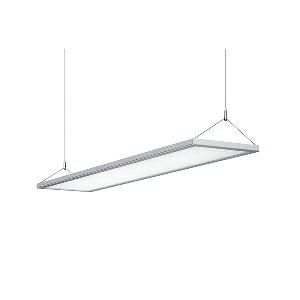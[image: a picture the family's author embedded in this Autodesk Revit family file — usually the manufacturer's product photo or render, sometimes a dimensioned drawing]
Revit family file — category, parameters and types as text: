
# Revit family: idoo_pendant_-_ipp_7000_840_d_00688760_aaad
name_source: partatom
category: Lighting Fixtures
units: mm (PartAtom-declared; Revit-internal decimal feet)

## family parameters
Cut with Voids When Loaded = No
Host = Face
Light Source = No
Part Type = Normal
Room Calculation Point = No
Round Connector Dimension = Use Diameter
Shared = No

## types (1)
- IDOO.pendant - IPP 7000/840/D (1 x LED, 7000 lm, 4000K)
    Apparent Load = 49 VA
    Approval mark = CE
    CIE Flux Codes = 55 85 96 33 100
    Color Rendering = 80-89
    Color Temperature = 4000K
    Control Gear = Electronic ballast
    Default Elevation = 1800 mm
    Description = IPP 7000/840/D|Suspended luminaire|light source: LED|connected load: 220-240V, 50/60Hz|Power consumption: approx. 49 W|standby: approx. 0,30|luminous flux: 7000 lm|luminous efficacy: 142 lm/W|light distribution: Direct/indirect|direct ratio: approx. 34 %|colour temperature: Cold white, ca. 4000 K|color rendering index (CRI): >= 80|chromaticity tolerance:  3 SDCM|System of protection: IP 20|technology: Continuously dimmable|luminaire body|material: |colour: White|lamp cover: Acrylic (PMMA), Clear|mains lead: 1.00 m With free stranded wires|Fastening: Steel cable 0.3 - 0.7 m|glare control: Prism aperture|luminance(L65): <= 2500 cd/m|unified glare rating(4H 8H): <=  16|special features: DALI - dimming via digital rotary dimmer, DALI Load 1x, Direct light component with edge light and light-guide technology for homogenous light exit, Integration into DALI light management systems, Indirect light component with Batwing diffuser for wide-beam light exit, TouchDIM - dimming via standard switch|Approval mark: VDE - ENEC|
    Height = 30 mm  [stored 0.0984252 ft]
    Lamp = 1 x LED
    Lamp Light Flux = 7000 lm
    Lamp count = 1
    Length = 1200 mm
    Luminous efficacy = 143 lm/W
    Manufacturer = Waldmann
    ModVariant = No
    Model = 00688760
    Mounting Place = Ceiling
    Mounting Type = Pendant
    Number of Poles = 1
    OnlyDefault = Yes
    Power Factor = 1
    Product Name = IDOO.pendant - IPP 7000/840/D
    Product group = Suspended luminaire
    ProductGroupID = 9
    Protection Class = Protection class I
    Protection Degree = IP 20
    RLX_Detail_Level = 1
    RLX_Emergency_Light_Flux = 0 lm
    RLX_Emergency_Type = 0
    RLX_Emergency_Type_DB = No
    RlxData = <blob elided: 23821 chars, md5=3d8b84b0>
    Socket = socket
    Standby Power = 0 W
    System Light Flux = 7000 lm
    System Power = 49 W
    Type Comments = Product without accessories
    Type Image = 113263000-00688760.jpg
    URL = http://relux.com
    VarID = ---
    Voltage = 230 V
    Voltage Range = 220-240 V
    Weight = 0.00 kg
    Width = 250 mm

note: [stored X ft] marks values corroborated as IEEE doubles in the binary element streams (Revit-internal decimal feet)

## geometry (parser evidence)
native form markers: Blend x4, Sweep x11
no freeform markers — native parametric forms only
